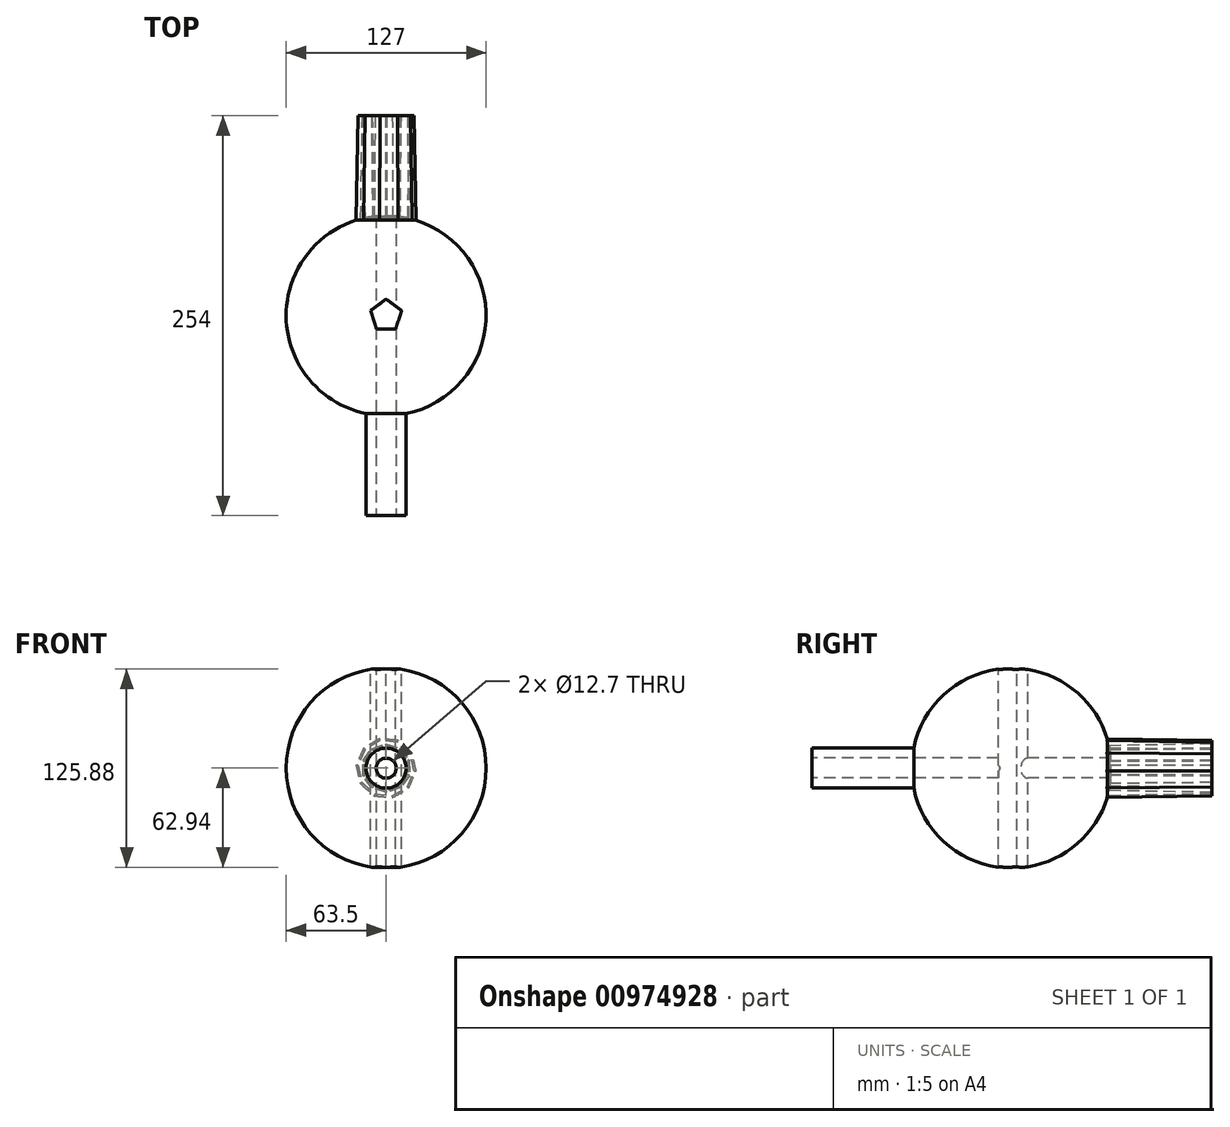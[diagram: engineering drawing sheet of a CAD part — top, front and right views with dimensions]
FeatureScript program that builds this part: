
annotation { "Feature Type Name" : "Feature", "Feature Type Description" : "" }
export const myFeature = defineFeature(function(context is Context, id is Id, definition is map)
    precondition{}
    {
        {
            var Q0;
            Q0=qCreatedBy(makeId("Front.planeOp"),FACE);
            var sketch = newSketch(context, id + "F0", { "sketchPlane" : qUnion([Q0])});
            skCircle(sketch, "E0", {"center": v(0, 0) * mm, "radius": 63.5 * mm});
            skLineSegment(sketch, "E1", {"start": v(0, 63.5) * mm, "end": v(0, -63.5) * mm});
            skSolve(sketch);
        }
        {
            var Q0;
            {var subQ0=sQuery(id+"F0.wireOp",EDGE,"E1");Q0=makeQuery(id+"F0.imprint","IMPRINT",FACE,{"disambiguationData":[TD([[makeQuery(id+"F0.imprint","IMPRINT",EDGE,{"derivedFrom":subQ0}),1.0]])]});}
            var Q1;
            Q1=sQuery(id+"F0.wireOp",EDGE,"E1");
            revolve(context, id + "F1", {"surfaceOperationType" : NewSurfaceOperationType.NEW, "entities" : qUnion([Q0]), "axis" : qUnion([Q1]), "revolveType" : RevolveType.FULL});
        }
        {
            var Q0;
            Q0=qCreatedBy(makeId("Front.planeOp"),FACE);
            var sketch = newSketch(context, id + "F2", { "sketchPlane" : qUnion([Q0])});
            skCircle(sketch, "E2", {"center": v(0, 0) * mm, "radius": 12.7 * mm});
            skSolve(sketch);
        }
        {
            var Q0;
            Q0 = qSketchRegion(id + "F2", true);
            extrude(context, id + "F3", {"entities" : qUnion([Q0]), "operationType" : NewBodyOperationType.ADD, "depth" : 127 * mm, "offsetDistance" : 25.4 * mm});
        }
        {
            var Q0;
            Q0=qCreatedBy(makeId("Front.planeOp"),FACE);
            var sketch = newSketch(context, id + "F4", { "sketchPlane" : qUnion([Q0])});
            skCircle(sketch, "E3", {"center": v(0, 0) * mm, "radius": 6.35 * mm});
            skSolve(sketch);
        }
        {
            var Q0;
            Q0 = qSketchRegion(id + "F4", true);
            extrude(context, id + "F5", {"entities" : qUnion([Q0]), "operationType" : NewBodyOperationType.REMOVE, "endBound" : BoundingType.SYMMETRIC, "oppositeDirection" : true, "depth" : 254 * mm, "offsetDistance" : 25.4 * mm});
        }
        {
            var Q0;
            Q0=qCreatedBy(makeId("Front.planeOp"),FACE);
            var sketch = newSketch(context, id + "F6", { "sketchPlane" : qUnion([Q0])});
            skCircle(sketch, "E4.cCircle", {"center": v(0, 0) * mm, "radius": 19.27 * mm, "construction": true});
            skLineSegment(sketch, "E4.0", {"start": v(-8.03, -18.6) * mm, "end": v(-17.43, -10.32) * mm});
            skLineSegment(sketch, "E4.1", {"start": v(-17.43, -10.32) * mm, "end": v(-20.17, 1.9) * mm});
            skLineSegment(sketch, "E4.2", {"start": v(-20.17, 1.9) * mm, "end": v(-15.2, 13.39) * mm});
            skLineSegment(sketch, "E4.3", {"start": v(-15.2, 13.39) * mm, "end": v(-4.43, 19.77) * mm});
            skLineSegment(sketch, "E4.4", {"start": v(-4.43, 19.77) * mm, "end": v(8.03, 18.6) * mm});
            skLineSegment(sketch, "E4.5", {"start": v(8.03, 18.6) * mm, "end": v(17.43, 10.32) * mm});
            skLineSegment(sketch, "E4.6", {"start": v(17.43, 10.32) * mm, "end": v(20.17, -1.9) * mm});
            skLineSegment(sketch, "E4.7", {"start": v(20.17, -1.9) * mm, "end": v(15.2, -13.39) * mm});
            skLineSegment(sketch, "E4.8", {"start": v(15.2, -13.39) * mm, "end": v(4.43, -19.77) * mm});
            skLineSegment(sketch, "E4.9", {"start": v(4.43, -19.77) * mm, "end": v(-8.03, -18.6) * mm});
            skPoint(sketch, "E4.0.midPoint", {"position": v(-12.73, -14.46) * mm});
            skLineSegment(sketch, "E5", {"start": v(-4.43, 19.77) * mm, "end": v(4.43, -19.77) * mm});
            skCircle(sketch, "E6.cCircle", {"center": v(0, 0) * mm, "radius": 12.48 * mm, "construction": true});
            skLineSegment(sketch, "E6.0", {"start": v(0.27, -13.12) * mm, "end": v(-7.5, -10.77) * mm});
            skLineSegment(sketch, "E6.1", {"start": v(-7.5, -10.77) * mm, "end": v(-12.4, -4.3) * mm});
            skLineSegment(sketch, "E6.2", {"start": v(-12.4, -4.3) * mm, "end": v(-12.56, 3.8) * mm});
            skLineSegment(sketch, "E6.3", {"start": v(-12.56, 3.8) * mm, "end": v(-7.93, 10.46) * mm});
            skLineSegment(sketch, "E6.4", {"start": v(-7.93, 10.46) * mm, "end": v(-0.27, 13.12) * mm});
            skLineSegment(sketch, "E6.5", {"start": v(-0.27, 13.12) * mm, "end": v(7.5, 10.77) * mm});
            skLineSegment(sketch, "E6.6", {"start": v(7.5, 10.77) * mm, "end": v(12.4, 4.3) * mm});
            skLineSegment(sketch, "E6.7", {"start": v(12.4, 4.3) * mm, "end": v(12.56, -3.8) * mm});
            skLineSegment(sketch, "E6.8", {"start": v(12.56, -3.8) * mm, "end": v(7.93, -10.46) * mm});
            skLineSegment(sketch, "E6.9", {"start": v(7.93, -10.46) * mm, "end": v(0.27, -13.12) * mm});
            skPoint(sketch, "E6.0.midPoint", {"position": v(-3.62, -11.95) * mm});
            skSolve(sketch);
        }
        {
            var Q0;
            Q0 = qSketchRegion(id + "F6", true);
            extrude(context, id + "F7", {"entities" : qUnion([Q0]), "operationType" : NewBodyOperationType.ADD, "oppositeDirection" : true, "depth" : 127 * mm, "offsetDistance" : 25.4 * mm, "hasDraft" : true, "draftAngle" : 1 * degree, "draftPullDirection" : true});
        }
        {
            var Q0;
            Q0=qCreatedBy(makeId("Top.planeOp"),FACE);
            var sketch = newSketch(context, id + "F8", { "sketchPlane" : qUnion([Q0])});
            skCircle(sketch, "E7.cCircle", {"center": v(0, 0) * mm, "radius": 8.38 * mm, "construction": true});
            skLineSegment(sketch, "E7.0", {"start": v(6.1, -8.38) * mm, "end": v(-6.1, -8.38) * mm});
            skLineSegment(sketch, "E7.1", {"start": v(-6.1, -8.38) * mm, "end": v(-9.86, 3.2) * mm});
            skLineSegment(sketch, "E7.2", {"start": v(-9.86, 3.2) * mm, "end": v(0, 10.36) * mm});
            skLineSegment(sketch, "E7.3", {"start": v(0, 10.36) * mm, "end": v(9.86, 3.2) * mm});
            skLineSegment(sketch, "E7.4", {"start": v(9.86, 3.2) * mm, "end": v(6.1, -8.38) * mm});
            skPoint(sketch, "E7.0.midPoint", {"position": v(0, -8.38) * mm});
            skSolve(sketch);
        }
        {
            var Q0;
            Q0 = qSketchRegion(id + "F8", true);
            extrude(context, id + "F9", {"entities" : qUnion([Q0]), "operationType" : NewBodyOperationType.REMOVE, "endBound" : BoundingType.SYMMETRIC, "oppositeDirection" : true, "depth" : 127 * mm, "offsetDistance" : 25.4 * mm});
        }
    });
